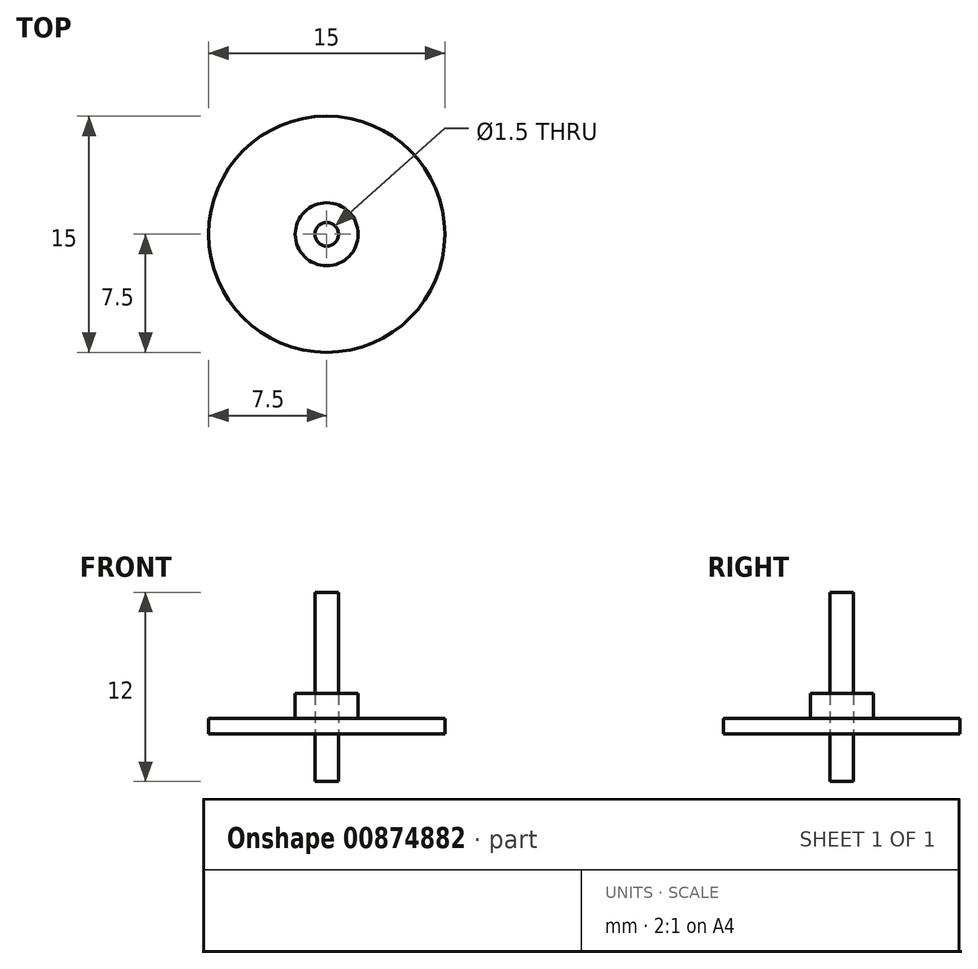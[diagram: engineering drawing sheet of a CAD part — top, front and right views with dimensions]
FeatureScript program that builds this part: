
annotation { "Feature Type Name" : "Feature", "Feature Type Description" : "" }
export const myFeature = defineFeature(function(context is Context, id is Id, definition is map)
    precondition{}
    {
        {
            var Q0;
            Q0=qCreatedBy(makeId("Top.planeOp"),FACE);
            var sketch = newSketch(context, id + "F0", { "sketchPlane" : qUnion([Q0])});
            skCircle(sketch, "E0", {"center": v(0, 0) * mm, "radius": 7.5 * mm});
            skCircle(sketch, "E1", {"center": v(0, 0) * mm, "radius": 2 * mm});
            skCircle(sketch, "E2", {"center": v(0, 0) * mm, "radius": 0.75 * mm});
            skSolve(sketch);
        }
        {
            var Q0;
            Q0=makeQuery(id+"F0.imprint","IMPRINT",FACE,{"disambiguationData":[TD([[makeQuery(id+"F0.imprint","IMPRINT",EDGE,{"derivedFrom":sQuery(id+"F0.wireOp",EDGE,"E0")}),1.0]])]});
            extrude(context, id + "F1", {"entities" : qUnion([Q0]), "depth" : 1 * mm, "offsetDistance" : 25 * mm});
        }
        {
            var Q0;
            Q0=makeQuery(id+"F0.imprint","IMPRINT",FACE,{"disambiguationData":[TD([[makeQuery(id+"F0.imprint","IMPRINT",EDGE,{"derivedFrom":sQuery(id+"F0.wireOp",EDGE,"E1")}),1.0]])]});
            extrude(context, id + "F2", {"entities" : qUnion([Q0]), "operationType" : NewBodyOperationType.ADD, "depth" : 2.6 * mm, "offsetDistance" : 25 * mm});
        }
        {
            var Q0;
            Q0=makeQuery(id+"F0.imprint","IMPRINT",FACE,{"disambiguationData":[TD([[makeQuery(id+"F0.imprint","IMPRINT",EDGE,{"derivedFrom":sQuery(id+"F0.wireOp",EDGE,"E2")}),1.0]])]});
            extrude(context, id + "F3", {"entities" : qUnion([Q0]), "depth" : 9 * mm, "offsetDistance" : 25 * mm, "hasSecondDirection" : true, "secondDirectionOppositeDirection" : true, "secondDirectionDepth" : 3 * mm});
        }
    });
